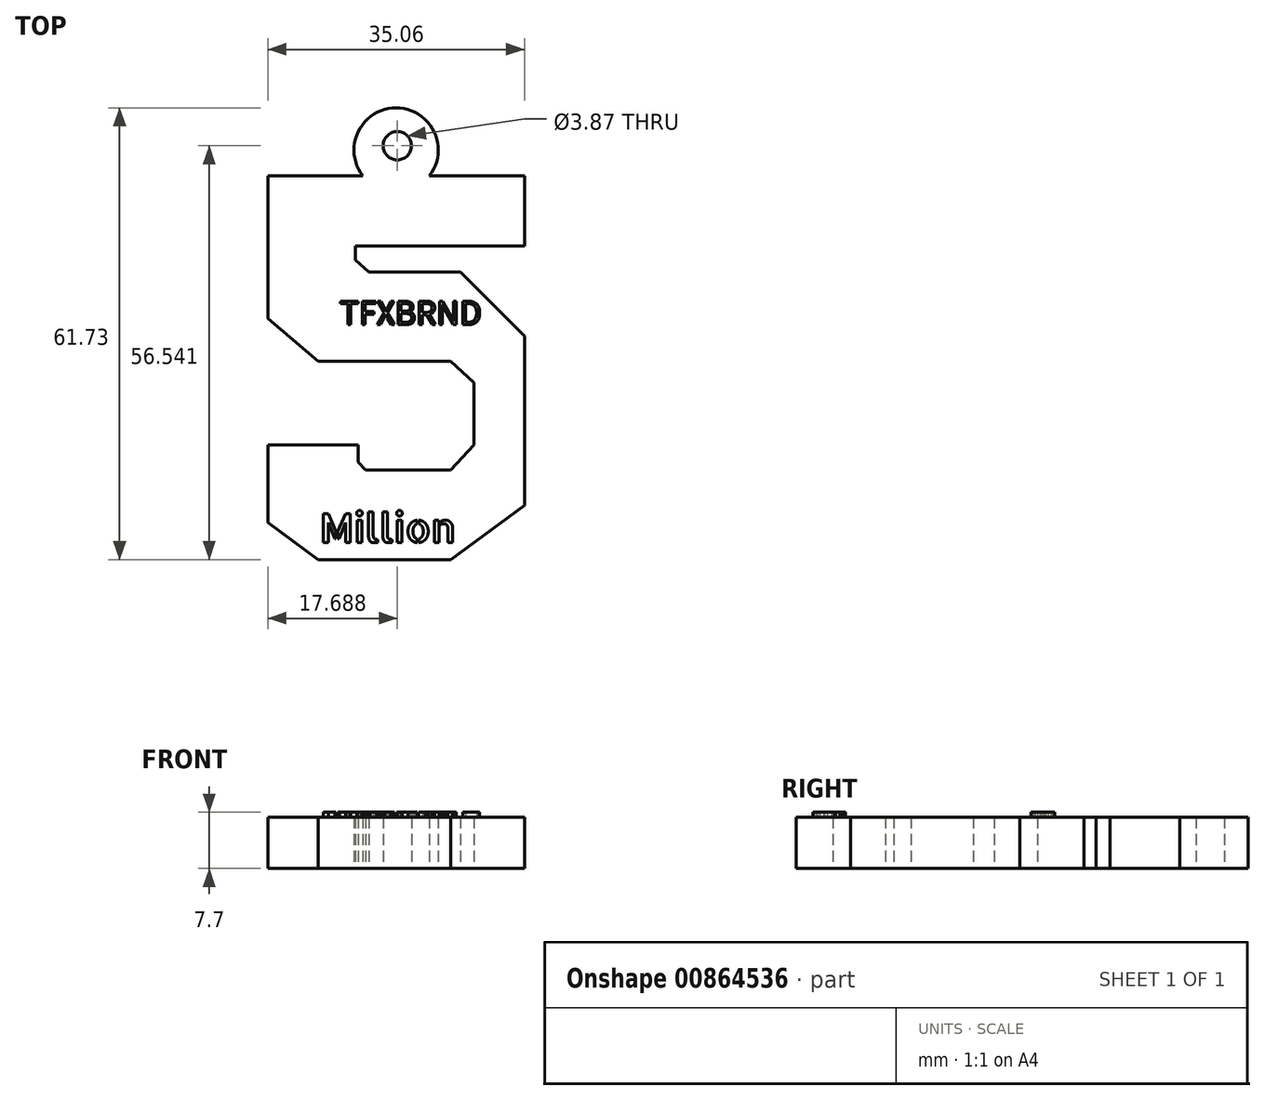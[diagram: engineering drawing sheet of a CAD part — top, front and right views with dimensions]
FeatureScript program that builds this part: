
annotation { "Feature Type Name" : "Feature", "Feature Type Description" : "" }
export const myFeature = defineFeature(function(context is Context, id is Id, definition is map)
    precondition{}
    {
        {
            var Q0;
            Q0=qCreatedBy(makeId("Top.planeOp"),FACE);
            var sketch = newSketch(context, id + "F0", { "sketchPlane" : qUnion([Q0])});
            skLineSegment(sketch, "E0", {"start": v(-9.83, 21.87) * mm, "end": v(-9.83, 2.4) * mm});
            skLineSegment(sketch, "E1", {"start": v(-9.83, 2.4) * mm, "end": v(-2.92, -3.45) * mm});
            skLineSegment(sketch, "E2", {"start": v(-2.92, -3.45) * mm, "end": v(15.14, -3.45) * mm});
            skLineSegment(sketch, "E3", {"start": v(15.14, -3.45) * mm, "end": v(18.33, -6.37) * mm});
            skLineSegment(sketch, "E4", {"start": v(18.33, -6.37) * mm, "end": v(18.33, -14.87) * mm});
            skLineSegment(sketch, "E5", {"start": v(18.33, -14.87) * mm, "end": v(15.14, -18.33) * mm});
            skLineSegment(sketch, "E6", {"start": v(-9.83, -14.87) * mm, "end": v(-9.83, -25.5) * mm});
            skLineSegment(sketch, "E7", {"start": v(-9.83, -25.5) * mm, "end": v(-2.92, -30.54) * mm});
            skLineSegment(sketch, "E8", {"start": v(-2.92, -30.54) * mm, "end": v(15.14, -30.54) * mm});
            skLineSegment(sketch, "E9", {"start": v(15.14, -30.54) * mm, "end": v(25.23, -23.1) * mm});
            skLineSegment(sketch, "E10", {"start": v(25.23, -23.1) * mm, "end": v(25.23, 0) * mm});
            skLineSegment(sketch, "E11", {"start": v(16.46, 8.76) * mm, "end": v(3.98, 8.76) * mm});
            skLineSegment(sketch, "E12", {"start": v(3.98, 8.76) * mm, "end": v(2.12, 10.4) * mm});
            skLineSegment(sketch, "E13", {"start": v(2.12, 10.4) * mm, "end": v(2.12, 12.33) * mm});
            skLineSegment(sketch, "E14", {"start": v(2.12, 12.33) * mm, "end": v(25.23, 12.33) * mm});
            skLineSegment(sketch, "E15", {"start": v(25.23, 12.33) * mm, "end": v(25.23, 21.87) * mm});
            skLineSegment(sketch, "E16", {"start": v(25.23, 21.87) * mm, "end": v(12.23, 21.87) * mm});
            skPoint(sketch, "E17.start.orphan", {"position": v(3.98, -14.87) * mm});
            skLineSegment(sketch, "E18", {"start": v(15.14, -18.33) * mm, "end": v(3.5, -18.33) * mm});
            skLineSegment(sketch, "E19", {"start": v(3.5, -18.33) * mm, "end": v(2.5, -17.24) * mm});
            skLineSegment(sketch, "E20", {"start": v(2.5, -17.24) * mm, "end": v(2.5, -14.87) * mm});
            skLineSegment(sketch, "E21", {"start": v(2.5, -14.87) * mm, "end": v(-9.83, -14.87) * mm});
            skLineSegment(sketch, "E22", {"start": v(25.23, 0) * mm, "end": v(16.46, 8.76) * mm});
            skPoint(sketch, "E23.orphan", {"position": v(18.33, 8.76) * mm});
            skArc(sketch, "E24", {"start": v(12.23, 21.87) * mm, "mid": v(7.7, 31.19) * mm, "end": v(3.17, 21.87) * mm});
            skPoint(sketch, "E24.centerSnap0", {"position": v(7.7, 21.87) * mm});
            skLineSegment(sketch, "E25.trimOffspring", {"start": v(3.17, 21.87) * mm, "end": v(-9.83, 21.87) * mm});
            skSolve(sketch);
        }
        {
            var Q0;
            Q0 = qSketchRegion(id + "F0", true);
            extrude(context, id + "F1", {"entities" : qUnion([Q0]), "depth" : 7 * mm, "offsetDistance" : 25 * mm});
        }
        {
            var Q0;
            Q0=qCreatedBy(makeId("Top.planeOp"),FACE);
            var sketch = newSketch(context, id + "F2", { "sketchPlane" : qUnion([Q0])});
            skCircle(sketch, "E26", {"center": v(7.86, 26) * mm, "radius": 1.93 * mm});
            skSolve(sketch);
        }
        {
            var Q0;
            Q0 = qSketchRegion(id + "F2", true);
            extrude(context, id + "F3", {"entities" : qUnion([Q0]), "operationType" : NewBodyOperationType.REMOVE, "depth" : 23 * mm, "offsetDistance" : 25 * mm});
        }
        {
            var Q0;
            Q0=qCreatedBy(makeId("Top.planeOp"),FACE);
            var sketch = newSketch(context, id + "F4", { "sketchPlane" : qUnion([Q0])});
            skText(sketch, "E27", { "text": "Million", "fontName": "AllertaStencil-Regular.ttf"});
            const initialGuessF4  = {"E27": [-0.00272, -0.0282, 1, 0, 0.00395]};
            skSetInitialGuess(sketch, initialGuessF4);
            skSolve(sketch);
        }
        {
            var Q0;
            Q0 = qSketchRegion(id + "F4", true);
            extrude(context, id + "F5", {"entities" : qUnion([Q0]), "operationType" : NewBodyOperationType.ADD, "depth" : 7.7 * mm, "offsetDistance" : 25 * mm});
        }
        {
            var Q0;
            Q0=qCreatedBy(makeId("Top.planeOp"),FACE);
            var sketch = newSketch(context, id + "F6", { "sketchPlane" : qUnion([Q0])});
            skText(sketch, "E28", { "text": "TFXBRND", "fontName": "NotoSansCJKjp-Regular.otf"});
            const initialGuessF6  = {"E28": [0, 0.00155, 1, 0, 0.00315]};
            skSetInitialGuess(sketch, initialGuessF6);
            skSolve(sketch);
        }
        {
            var Q0;
            Q0 = qSketchRegion(id + "F6", true);
            extrude(context, id + "F7", {"entities" : qUnion([Q0]), "operationType" : NewBodyOperationType.ADD, "depth" : 7.7 * mm, "offsetDistance" : 25 * mm});
        }
    });
